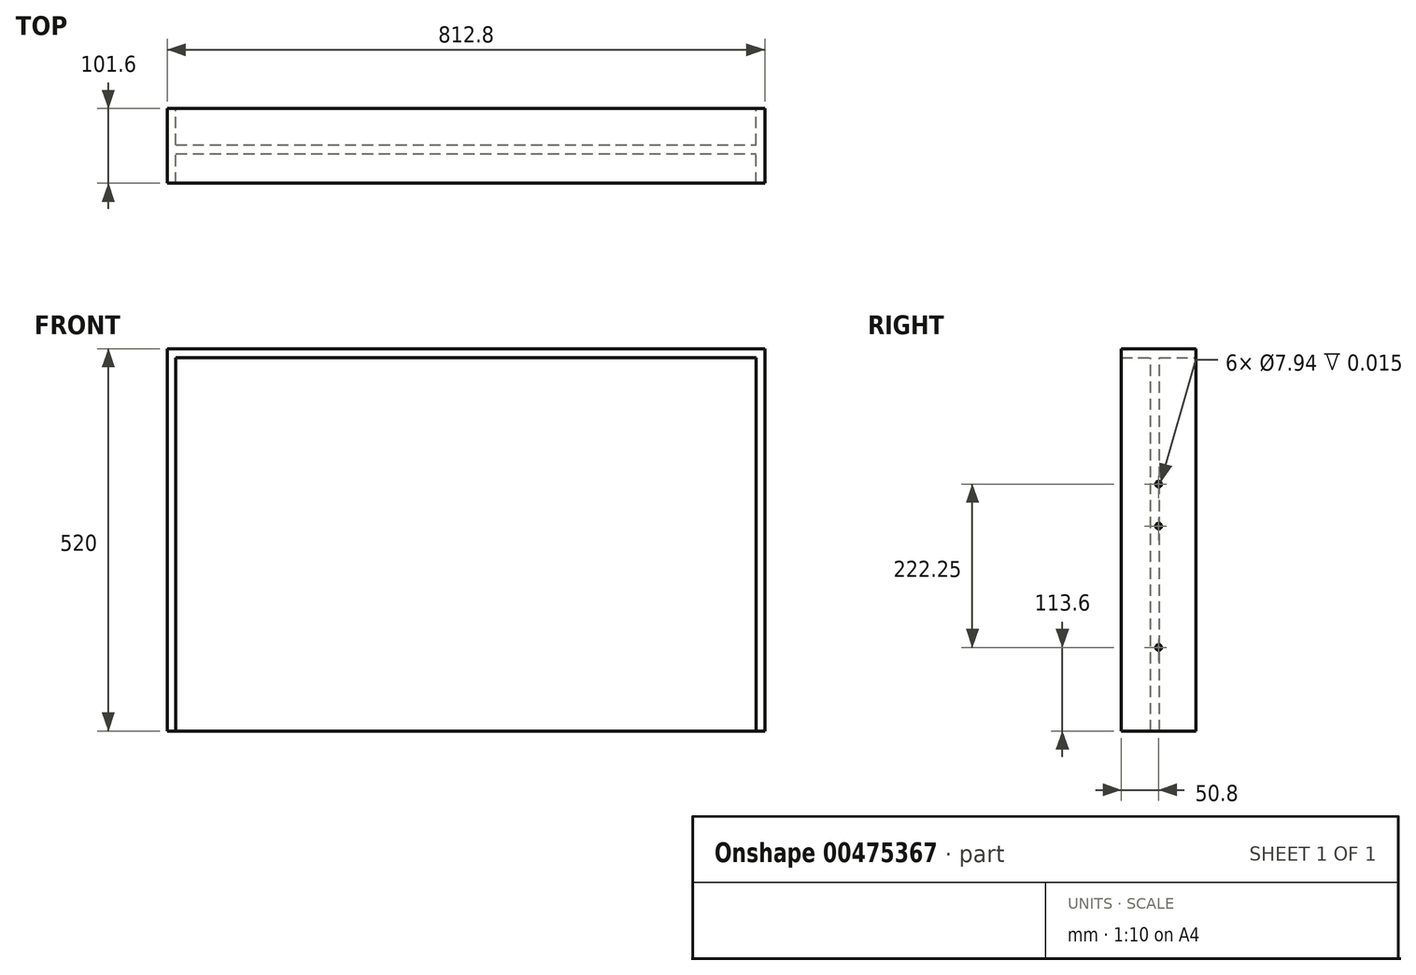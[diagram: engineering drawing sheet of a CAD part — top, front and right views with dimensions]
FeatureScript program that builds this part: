
annotation { "Feature Type Name" : "Feature", "Feature Type Description" : "" }
export const myFeature = defineFeature(function(context is Context, id is Id, definition is map)
    precondition{}
    {
        {
            var Q0;
            Q0=qCreatedBy(makeId("Top.planeOp"),FACE);
            var sketch = newSketch(context, id + "F0", { "sketchPlane" : qUnion([Q0])});
            skLineSegment(sketch, "E0.bottom", {"start": v(0, 0) * mm, "end": v(812.8, 0) * mm});
            skLineSegment(sketch, "E0.top", {"start": v(0, 101.6) * mm, "end": v(812.8, 101.6) * mm});
            skLineSegment(sketch, "E0.left", {"start": v(0, 0) * mm, "end": v(0, 101.6) * mm});
            skLineSegment(sketch, "E0.right", {"start": v(812.8, 0) * mm, "end": v(812.8, 101.6) * mm});
            skSolve(sketch);
        }
        {
            var Q0;
            Q0 = qSketchRegion(id + "F0", true);
            extrude(context, id + "F1", {"entities" : qUnion([Q0]), "depth" : 12 * mm});
        }
        {
            var Q0;
            Q0=makeQuery(id+"F1.opExtrude","CAP_FACE",FACE,{"disambiguationData":[OSD([sQuery(id+"F0.wireOp",EDGE,"E0.bottom"),sQuery(id+"F0.wireOp",EDGE,"E0.top"),sQuery(id+"F0.wireOp",EDGE,"E0.left"),sQuery(id+"F0.wireOp",EDGE,"E0.right")])],"isStart":true});
            var sketch = newSketch(context, id + "F2", { "sketchPlane" : qUnion([Q0])});
            skLineSegment(sketch, "E1.0", {"start": v(0, 0) * mm, "end": v(0, -101.6) * mm});
            skLineSegment(sketch, "E1.1", {"start": v(812.8, 0) * mm, "end": v(812.8, -101.6) * mm});
            skLineSegment(sketch, "E2.0", {"start": v(12, 0) * mm, "end": v(12, -40.22) * mm});
            skLineSegment(sketch, "E3.0", {"start": v(800.8, 0) * mm, "end": v(800.8, -40.22) * mm});
            skLineSegment(sketch, "E4.0", {"start": v(12, -52.22) * mm, "end": v(800.8, -52.22) * mm});
            skLineSegment(sketch, "E5.0", {"start": v(12, -40.22) * mm, "end": v(800.8, -40.22) * mm});
            skLineSegment(sketch, "E6", {"start": v(0, 0) * mm, "end": v(12, 0) * mm});
            skLineSegment(sketch, "E7", {"start": v(0, -101.6) * mm, "end": v(12, -101.6) * mm});
            skLineSegment(sketch, "E8", {"start": v(800.8, 0) * mm, "end": v(812.8, 0) * mm});
            skLineSegment(sketch, "E9", {"start": v(800.8, -101.6) * mm, "end": v(812.8, -101.6) * mm});
            skPoint(sketch, "E10.trimOffspring.end.orphan", {"position": v(812.8, -50.8) * mm});
            skLineSegment(sketch, "E11.trimOffspring", {"start": v(800.8, -52.22) * mm, "end": v(800.8, -101.6) * mm});
            skLineSegment(sketch, "E12.trimOffspring", {"start": v(12, -52.22) * mm, "end": v(12, -101.6) * mm});
            skPoint(sketch, "E13.start.orphan", {"position": v(0, -50.8) * mm});
            skSolve(sketch);
        }
        {
            var Q0;
            Q0 = qSketchRegion(id + "F2", true);
            extrude(context, id + "F3", {"entities" : qUnion([Q0]), "operationType" : NewBodyOperationType.ADD, "depth" : 508 * mm});
        }
        {
            var Q0;
            Q0=makeQuery(id+"F3.boolean.opBoolean","MERGE",FACE,{"derivedFrom":[makeQuery(id+"F1.opExtrude","SWEPT_FACE",FACE,{"disambiguationData":[OSD([sQuery(id+"F0.wireOp",EDGE,"E0.right")])]}),makeQuery(id+"F3.opExtrude","SWEPT_FACE",FACE,{"disambiguationData":[OSD([sQuery(id+"F2.wireOp",EDGE,"E1.1")])]})]});
            var sketch = newSketch(context, id + "F4", { "sketchPlane" : qUnion([Q0])});
            skLineSegment(sketch, "E14", {"start": v(50.8, 12) * mm, "end": v(50.8, -508) * mm, "construction": true});
            skCircle(sketch, "E15", {"center": v(50.8, -172.15) * mm, "radius": 3.97 * mm});
            skCircle(sketch, "E16", {"center": v(50.8, -229.3) * mm, "radius": 3.97 * mm});
            skCircle(sketch, "E17", {"center": v(50.8, -394.4) * mm, "radius": 3.97 * mm});
            skSolve(sketch);
        }
        {
            var Q0;
            Q0 = qSketchRegion(id + "F4", true);
            extrude(context, id + "F5", {"entities" : qUnion([Q0]), "operationType" : NewBodyOperationType.REMOVE, "oppositeDirection" : true, "depth" : 3 / 203.2 * mm});
        }
        {
            var Q0;
            Q0=makeQuery(id+"F3.boolean.opBoolean","MERGE",FACE,{"derivedFrom":[makeQuery(id+"F1.opExtrude","SWEPT_FACE",FACE,{"disambiguationData":[OSD([sQuery(id+"F0.wireOp",EDGE,"E0.left")])]}),makeQuery(id+"F3.opExtrude","SWEPT_FACE",FACE,{"disambiguationData":[OSD([sQuery(id+"F2.wireOp",EDGE,"E1.0")])]})]});
            var sketch = newSketch(context, id + "F6", { "sketchPlane" : qUnion([Q0])});
            skCircle(sketch, "E18.0", {"center": v(-50.8, -172.15) * mm, "radius": 3.97 * mm});
            skCircle(sketch, "E18.1", {"center": v(-50.8, -229.3) * mm, "radius": 3.97 * mm});
            skCircle(sketch, "E18.2", {"center": v(-50.8, -394.4) * mm, "radius": 3.97 * mm});
            skSolve(sketch);
        }
        {
            var Q0;
            Q0 = qSketchRegion(id + "F6", true);
            extrude(context, id + "F7", {"entities" : qUnion([Q0]), "operationType" : NewBodyOperationType.REMOVE, "oppositeDirection" : true, "depth" : 3 / 203.2 * mm});
        }
    });
